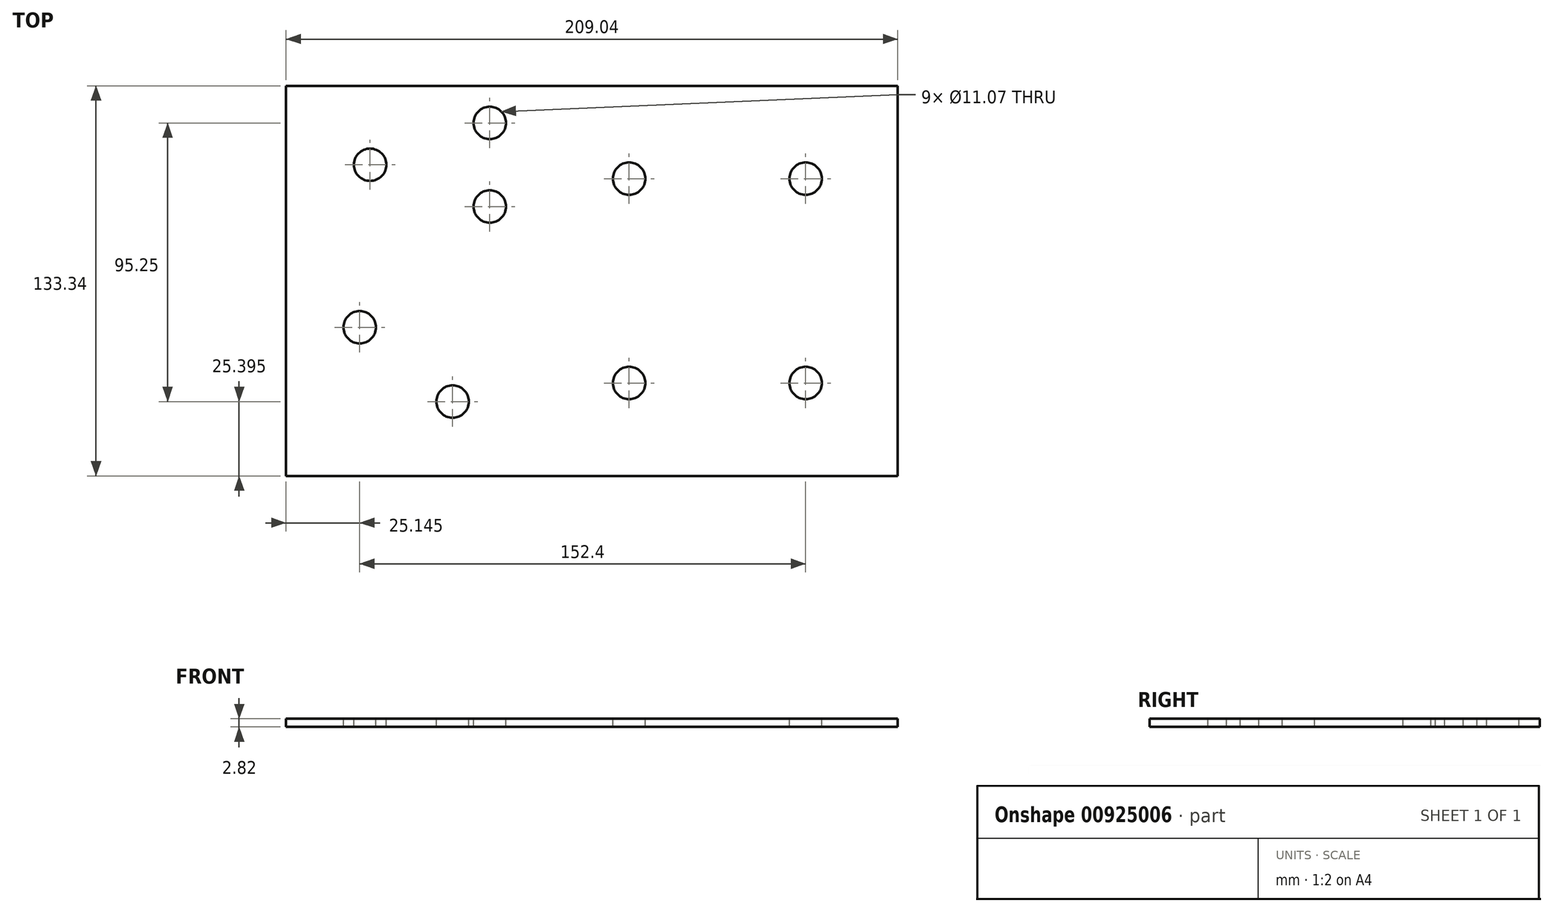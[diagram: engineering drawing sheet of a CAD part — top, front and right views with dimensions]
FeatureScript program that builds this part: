
annotation { "Feature Type Name" : "Feature", "Feature Type Description" : "" }
export const myFeature = defineFeature(function(context is Context, id is Id, definition is map)
    precondition{}
    {
        {
            var Q0;
            Q0=qCreatedBy(makeId("Top.planeOp"),FACE);
            var sketch = newSketch(context, id + "F0", { "sketchPlane" : qUnion([Q0])});
            skLineSegment(sketch, "E0.bottom", {"start": v(104.52, -66.67) * mm, "end": v(-104.52, -66.67) * mm});
            skLineSegment(sketch, "E0.top", {"start": v(104.52, 66.68) * mm, "end": v(-104.52, 66.67) * mm});
            skLineSegment(sketch, "E0.left", {"start": v(104.52, -66.67) * mm, "end": v(104.52, 66.68) * mm});
            skLineSegment(sketch, "E0.right", {"start": v(-104.52, -66.67) * mm, "end": v(-104.52, 66.68) * mm});
            skPoint(sketch, "E0.middle", {"position": v(0, 0) * mm});
            skSolve(sketch);
        }
        {
            var Q0;
            Q0=qSketchRegion(id+"F0",true);
            extrude(context, id + "F1", {"entities" : qUnion([Q0]), "depth" : 2.82 * mm, "offsetDistance" : 25.4 * mm});
        }
        {
            var Q0;
            Q0=makeQuery(id+"F1.opExtrude","CAP_FACE",FACE,{"disambiguationData":[OSD([sQuery(id+"F0.wireOp",EDGE,"E0.bottom"),sQuery(id+"F0.wireOp",EDGE,"E0.top"),sQuery(id+"F0.wireOp",EDGE,"E0.left"),sQuery(id+"F0.wireOp",EDGE,"E0.right")])],"isStart":false});
            var sketch = newSketch(context, id + "F2", { "sketchPlane" : qUnion([Q0])});
            skCircle(sketch, "E1", {"center": v(-75.82, 39.69) * mm, "radius": 5.54 * mm});
            skCircle(sketch, "E2", {"center": v(-79.38, -15.87) * mm, "radius": 5.54 * mm});
            skCircle(sketch, "E3", {"center": v(-34.93, 53.98) * mm, "radius": 5.54 * mm});
            skCircle(sketch, "E4", {"center": v(-34.93, 25.4) * mm, "radius": 5.54 * mm});
            skCircle(sketch, "E5", {"center": v(12.7, 34.93) * mm, "radius": 5.54 * mm});
            skCircle(sketch, "E6", {"center": v(-47.62, -41.28) * mm, "radius": 5.54 * mm});
            skCircle(sketch, "E7", {"center": v(73.02, 34.93) * mm, "radius": 5.54 * mm});
            skCircle(sketch, "E8", {"center": v(12.7, -34.92) * mm, "radius": 5.54 * mm});
            skCircle(sketch, "E9", {"center": v(73.03, -34.92) * mm, "radius": 5.54 * mm});
            skLineSegment(sketch, "E10", {"start": v(0, 66.68) * mm, "end": v(0, -66.68) * mm, "construction": true});
            skLineSegment(sketch, "E11", {"start": v(-104.52, 0) * mm, "end": v(104.52, 0) * mm, "construction": true});
            skLineSegment(sketch, "E12.bottom", {"start": v(101.35, -64.67) * mm, "end": v(-101.35, -64.67) * mm, "construction": true});
            skLineSegment(sketch, "E12.top", {"start": v(101.35, 64.67) * mm, "end": v(-101.35, 64.67) * mm, "construction": true});
            skLineSegment(sketch, "E12.left", {"start": v(101.35, -64.67) * mm, "end": v(101.35, 64.67) * mm, "construction": true});
            skLineSegment(sketch, "E12.right", {"start": v(-101.35, -64.67) * mm, "end": v(-101.35, 64.67) * mm, "construction": true});
            skPoint(sketch, "E12.middle", {"position": v(0, 0) * mm});
            skLineSegment(sketch, "E13", {"start": v(-21.46, 64.67) * mm, "end": v(-21.46, -64.67) * mm, "construction": true});
            skLineSegment(sketch, "E14", {"start": v(-46.86, 64.67) * mm, "end": v(-46.86, 0) * mm, "construction": true});
            skLineSegment(sketch, "E15", {"start": v(-50.04, 64.67) * mm, "end": v(-50.04, 0) * mm, "construction": true});
            skLineSegment(sketch, "E16", {"start": v(-104.52, 10.7) * mm, "end": v(104.52, 10.7) * mm, "construction": true});
            skLineSegment(sketch, "E17", {"start": v(-34.93, 53.98) * mm, "end": v(-34.93, 25.4) * mm, "construction": true});
            skPoint(sketch, "E18", {"position": v(-34.93, 39.69) * mm});
            skSolve(sketch);
        }
        {
            var Q0;
            Q0 = qSketchRegion(id + "F2", true);
            extrude(context, id + "F3", {"entities" : qUnion([Q0]), "operationType" : NewBodyOperationType.REMOVE, "endBound" : BoundingType.THROUGH_ALL, "oppositeDirection" : true, "depth" : 25.4 * mm, "offsetDistance" : 25.4 * mm});
        }
    });
